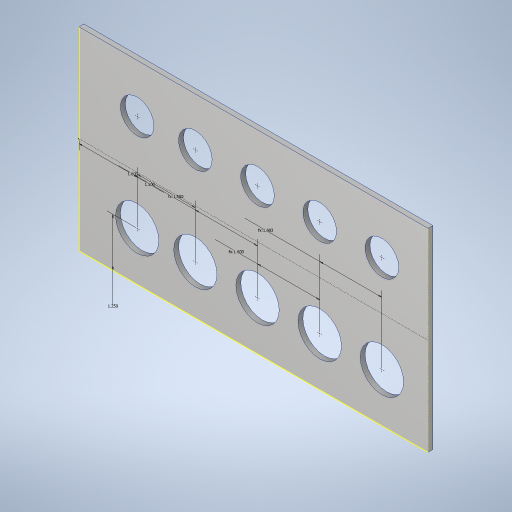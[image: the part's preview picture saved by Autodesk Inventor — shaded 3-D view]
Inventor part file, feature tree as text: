
AUTODESK INVENTOR PART (.ipt)
format: ipt  version: 2023.4 (Build 274418000, 418)  size: 283,648 bytes
history: native  units: in
note: dims shown in document units (in); Inventor stores cm internally (conversion verified against a paired STEP export)
features: hole x10, sketch x3, extrude x1
ambient origin geometry x8: Origin, YZ Plane, XZ Plane, XY Plane, X Axis, Y Axis, Z Axis, Center Point
bodies: Solid1 (feature_tree)
feature tree (14):
  extrude  "Extrusion1"  Depth=5.0in
  sketch  "Sketch2"  dims[d2=0.125in d3=0.0in d4=1.25in]
  hole  "Hole1"  [1 undecoded]
  hole  "Hole2"  [1 undecoded]
  hole  "Hole3"  [1 undecoded]
  hole  "Hole4"  [1 undecoded]
  hole  "Hole5"  [1 undecoded]
  sketch  "Sketch3"  dims[d5=1.5in d6=1.5in d7=1.603in d8=1.603in d9=1.603in d10=1.114in d11=0.75in d12=0.375in d13=0.25in d14=0.5635in d15=1.0in d16=0.8108in d17=1.115in d18=0.75in d19=0.375in d20=0.25in d21=0.5635in d22=1.0in d23=0.8108in d24=1.116in d25=0.75in d26=0.375in d27=0.25in d28=0.5635in d29=1.0in d30=0.8108in d31=1.121in d32=0.75in d33=0.375in d34=0.25in d35=0.5635in d36=1.0in d37=0.8108in d38=1.118in d39=0.75in d40=0.375in d41=0.25in d42=0.5635in d43=1.0in d44=0.8108in d45=0.865in d46=0.75in d47=0.375in d48=0.25in d49=0.5635in d50=1.0in d51=0.8108in d52=0.865in d53=0.75in d54=0.375in d55=0.25in d56=0.5635in d57=1.0in d58=0.8108in d59=0.866in d60=0.75in d61=0.375in d62=0.25in d63=0.5635in d64=1.0in d65=0.8108in d66=0.867in d67=0.75in d68=0.375in d69=0.25in d70=0.5635in d71=1.0in d72=0.8108in d73=0.868in d74=0.75in d75=0.375in d76=0.25in d77=0.5635in d78=1.0in d79=0.8108in]
  hole  "Hole6"  [1 undecoded]
  hole  "Hole7"  [1 undecoded]
  hole  "Hole8"  [1 undecoded]
  hole  "Hole9"  [1 undecoded]
  hole  "Hole10"  [1 undecoded]
  sketch  "Sketch1"  dims[d0=9.0in d1=5.0in]
note: 10 required parameter values undecoded (feature->parameter linkage not recoverable at this tier; creation-order binding heuristic only, values carry confidence <= 0.55)
